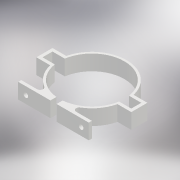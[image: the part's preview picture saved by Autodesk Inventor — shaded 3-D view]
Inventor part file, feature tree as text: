
AUTODESK INVENTOR PART (.ipt)
format: ipt  version: 2018.2 (Build 222227000, 227)  size: 177,664 bytes
history: native  units: mm
features: extrude x2, sketch x2, mirror x1
ambient origin geometry x8: Origin, YZ Plane, XZ Plane, XY Plane, X Axis, Y Axis, Z Axis, Center Point
bodies: Solid1 (feature_tree)
feature tree (5):
  extrude  "Extrusion1"  Depth=25.0mm
  extrude  "Extrusion2"  Depth=2.0mm
  mirror  "Mirror1"
  sketch  "Sketch1"  dims[d1=25.0mm d2=36.0mm]
  sketch  "Sketch2"  dims[d3=2.0mm d4=1.4mm d5=5.0mm d6=2.0mm d7=4.0mm d8=10.0mm d9=0.0mm d10=3.0mm d11=20.0mm d12=0.0mm d13=42.3mm d19=22.55mm d20=8.0mm d21=6.5mm d22=2.0mm d23=6.5mm d24=8.0mm d25=2.0mm d26=2.0mm d27=2.0mm]
